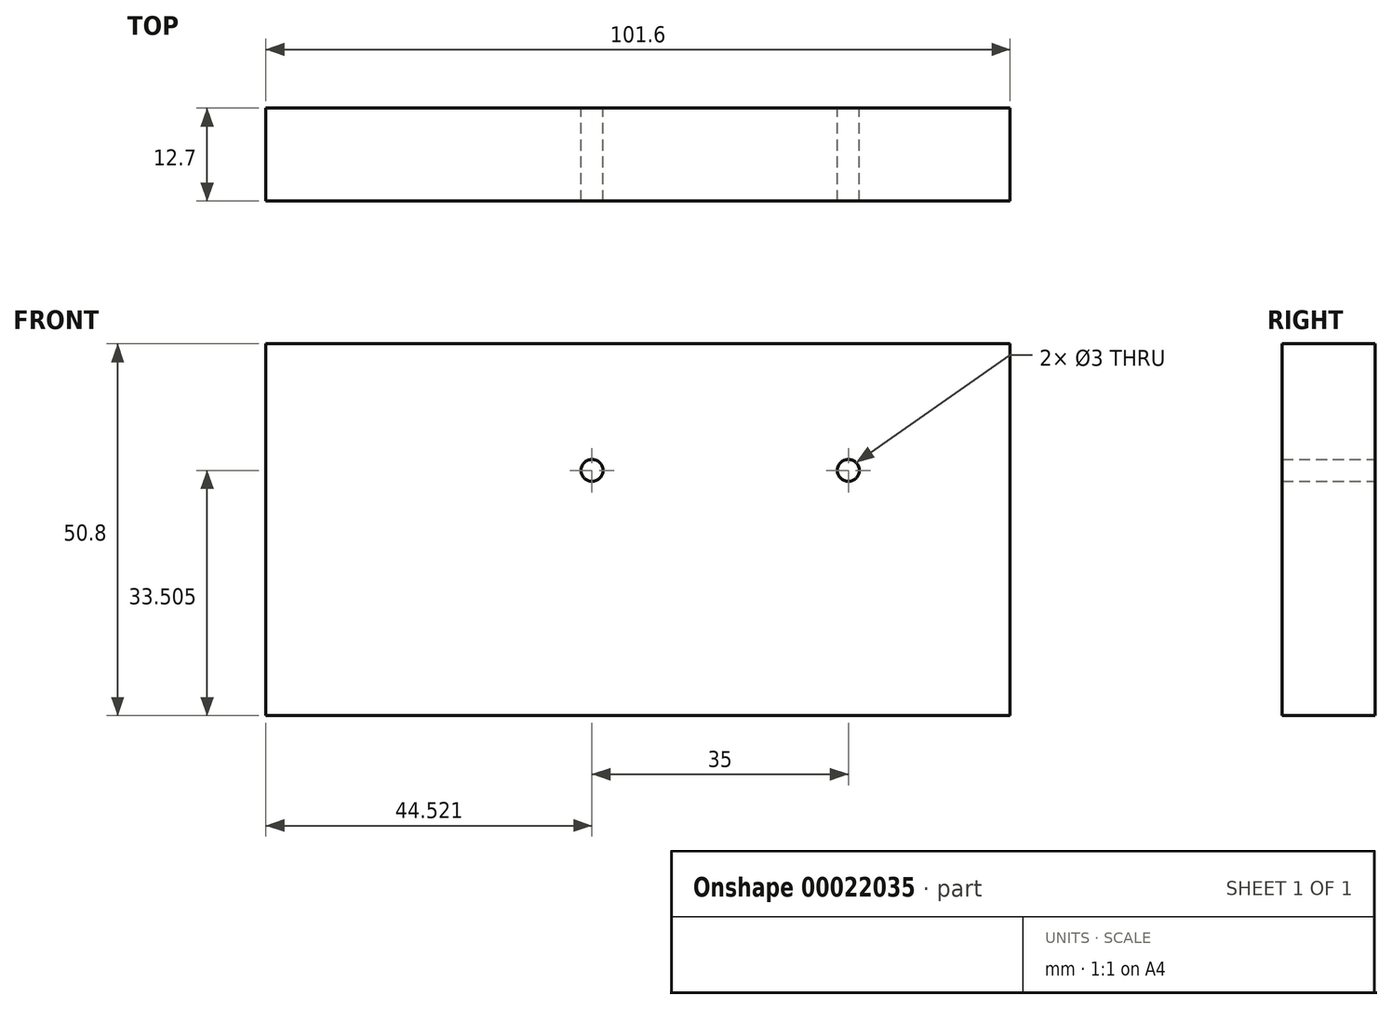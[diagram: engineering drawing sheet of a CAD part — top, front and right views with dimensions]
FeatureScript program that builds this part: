
annotation { "Feature Type Name" : "Feature", "Feature Type Description" : "" }
export const myFeature = defineFeature(function(context is Context, id is Id, definition is map)
    precondition{}
    {
        {
            var Q0;
            Q0=qCreatedBy(makeId("Front.planeOp"),FACE);
            var sketch = newSketch(context, id + "F0", { "sketchPlane" : qUnion([Q0])});
            skLineSegment(sketch, "E0.bottom", {"start": v(-73.94, 33.45) * mm, "end": v(27.66, 33.45) * mm});
            skLineSegment(sketch, "E0.top", {"start": v(-73.94, -17.35) * mm, "end": v(27.66, -17.35) * mm});
            skLineSegment(sketch, "E0.left", {"start": v(-73.94, 33.45) * mm, "end": v(-73.94, -17.35) * mm});
            skLineSegment(sketch, "E0.right", {"start": v(27.66, 33.45) * mm, "end": v(27.66, -17.35) * mm});
            skCircle(sketch, "E1", {"center": v(-29.42, 16.16) * mm, "radius": 1.5 * mm});
            skCircle(sketch, "E2", {"center": v(5.58, 16.16) * mm, "radius": 1.5 * mm});
            skCircle(sketch, "E3", {"center": v(30.58, 16.16) * mm, "radius": 1.5 * mm});
            skPoint(sketch, "E4.start.orphan", {"position": v(7.08, 16.16) * mm});
            skPoint(sketch, "E5.start.orphan", {"position": v(-63.42, 16.16) * mm});
            skPoint(sketch, "E6.start.orphan", {"position": v(-27.92, 16.16) * mm});
            skLineSegment(sketch, "E7", {"start": v(-29.42, 16.16) * mm, "end": v(5.58, 16.16) * mm});
            skLineSegment(sketch, "E8", {"start": v(5.58, 16.16) * mm, "end": v(30.58, 16.16) * mm});
            skSolve(sketch);
        }
        {
            var Q0;
            Q0=makeQuery(id+"F0.imprint","IMPRINT",FACE,{"disambiguationData":[TD([[makeQuery(id+"F0.imprint","IMPRINT",EDGE,{"derivedFrom":sQuery(id+"F0.wireOp",EDGE,"E0.bottom")}),-1.0]])]});
            extrude(context, id + "F1", {"entities" : qUnion([Q0]), "depth" : 12.7 * mm});
        }
    });
